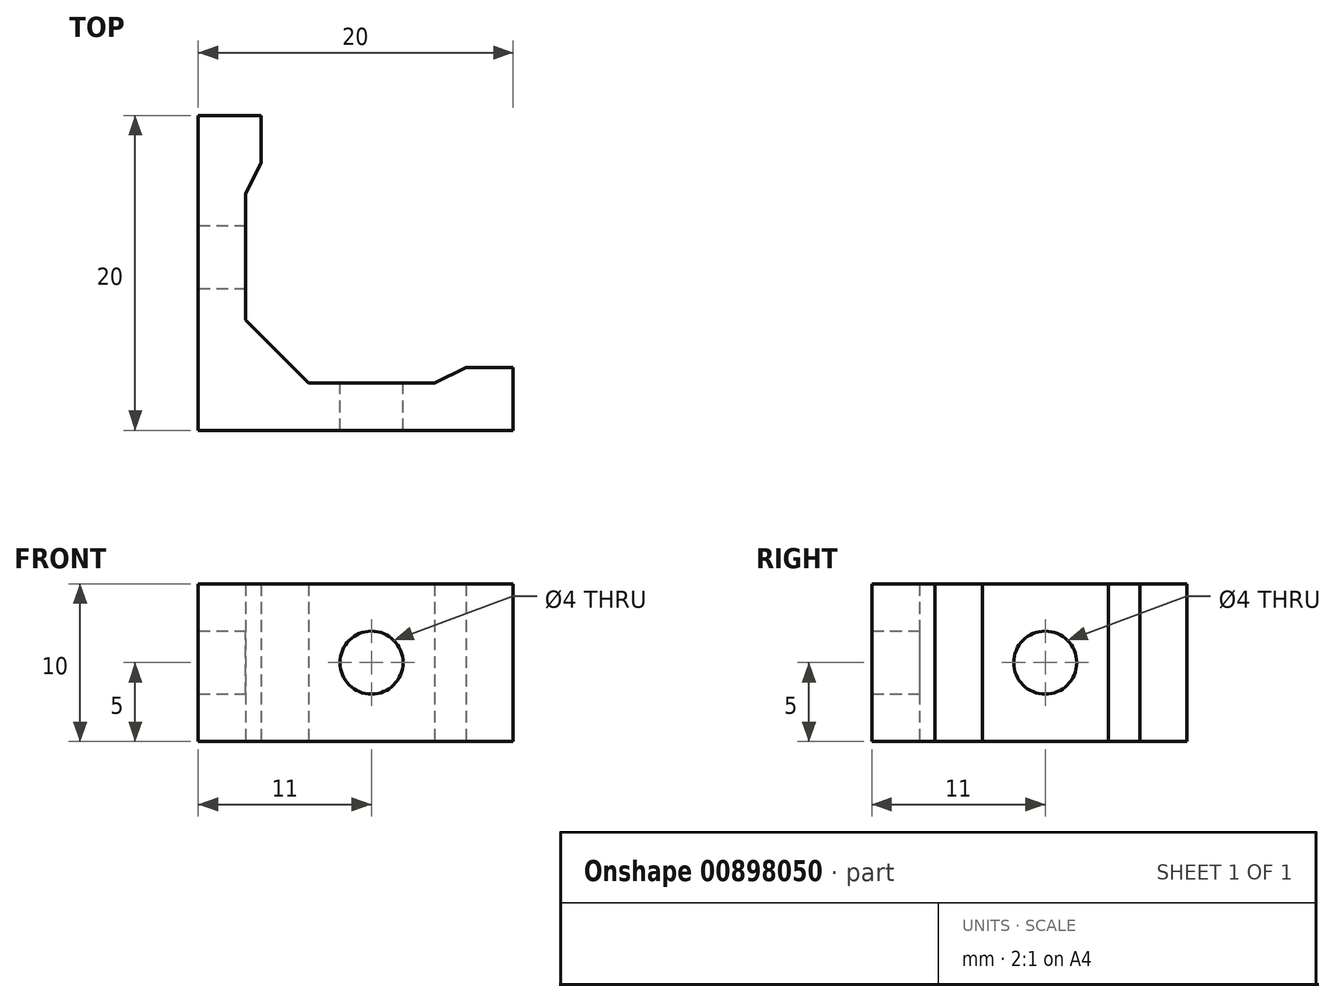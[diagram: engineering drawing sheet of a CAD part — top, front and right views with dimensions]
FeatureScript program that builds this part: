
annotation { "Feature Type Name" : "Feature", "Feature Type Description" : "" }
export const myFeature = defineFeature(function(context is Context, id is Id, definition is map)
    precondition{}
    {
        {
            var Q0;
            Q0=qCreatedBy(makeId("Top.planeOp"),FACE);
            var sketch = newSketch(context, id + "F0", { "sketchPlane" : qUnion([Q0])});
            skLineSegment(sketch, "E0", {"start": v(0, 0) * mm, "end": v(20, 0) * mm});
            skLineSegment(sketch, "E1", {"start": v(0, 0) * mm, "end": v(40, 40) * mm, "construction": true});
            skLineSegment(sketch, "E2", {"start": v(0, 0) * mm, "end": v(0, 40) * mm, "construction": true});
            skLineSegment(sketch, "E3", {"start": v(0, 40) * mm, "end": v(40, 40) * mm, "construction": true});
            skLineSegment(sketch, "E4", {"start": v(40, 40) * mm, "end": v(40, 0) * mm, "construction": true});
            skLineSegment(sketch, "E5", {"start": v(20, 0) * mm, "end": v(20, 4) * mm});
            skLineSegment(sketch, "E6", {"start": v(20, 4) * mm, "end": v(17, 4) * mm});
            skLineSegment(sketch, "E7", {"start": v(17, 4) * mm, "end": v(15, 3) * mm});
            skLineSegment(sketch, "E8", {"start": v(15, 3) * mm, "end": v(7, 3) * mm});
            skLineSegment(sketch, "E9", {"start": v(15, 3) * mm, "end": v(15, 0) * mm, "construction": true});
            skLineSegment(sketch, "E10", {"start": v(15, 3) * mm, "end": v(20, 3) * mm, "construction": true});
            skLineSegment(sketch, "E11", {"start": v(7, 3) * mm, "end": v(5, 5) * mm});
            skLineSegment(sketch, "E12.MirrorCS", {"start": v(3, 7) * mm, "end": v(5, 5) * mm});
            skLineSegment(sketch, "E13.MirrorCS", {"start": v(3, 15) * mm, "end": v(3, 7) * mm});
            skLineSegment(sketch, "E14.MirrorCS", {"start": v(4, 17) * mm, "end": v(3, 15) * mm});
            skLineSegment(sketch, "E15.MirrorCS", {"start": v(4, 20) * mm, "end": v(4, 17) * mm});
            skLineSegment(sketch, "E16.MirrorCS", {"start": v(0, 0) * mm, "end": v(0, 20) * mm});
            skLineSegment(sketch, "E17.MirrorCS", {"start": v(0, 20) * mm, "end": v(4, 20) * mm});
            skSolve(sketch);
        }
        {
            var Q0;
            Q0=makeQuery(id+"F0.imprint","IMPRINT",FACE,{"disambiguationData":[TD([[makeQuery(id+"F0.imprint","IMPRINT",EDGE,{"derivedFrom":sQuery(id+"F0.wireOp",EDGE,"E0")}),1.0]])]});
            extrude(context, id + "F1", {"entities" : qUnion([Q0]), "depth" : 10 * mm, "offsetDistance" : 25 * mm});
        }
        {
            var Q0;
            Q0=makeQuery(id+"F1.opExtrude","SWEPT_FACE",FACE,{"disambiguationData":[OSD([sQuery(id+"F0.wireOp",EDGE,"E13.MirrorCS")])]});
            var sketch = newSketch(context, id + "F2", { "sketchPlane" : qUnion([Q0])});
            skLineSegment(sketch, "E18", {"start": v(0, 0) * mm, "end": v(0, 5) * mm, "construction": true});
            skLineSegment(sketch, "E19", {"start": v(0, 5) * mm, "end": v(11, 5) * mm, "construction": true});
            skCircle(sketch, "E20", {"center": v(11, 5) * mm, "radius": 2 * mm});
            skSolve(sketch);
        }
        {
            var Q0;
            Q0=qSketchRegion(id+"F2",true);
            extrude(context, id + "F3", {"entities" : qUnion([Q0]), "operationType" : NewBodyOperationType.REMOVE, "oppositeDirection" : true, "depth" : 5 * mm, "offsetDistance" : 25 * mm});
        }
        {
            var Q0;
            Q0=makeQuery(id+"F1.opExtrude","SWEPT_FACE",FACE,{"disambiguationData":[OSD([sQuery(id+"F0.wireOp",EDGE,"E8")])]});
            var sketch = newSketch(context, id + "F4", { "sketchPlane" : qUnion([Q0])});
            skLineSegment(sketch, "E21", {"start": v(0, 0) * mm, "end": v(0, 5) * mm, "construction": true});
            skLineSegment(sketch, "E22", {"start": v(0, 5) * mm, "end": v(-11, 5) * mm, "construction": true});
            skCircle(sketch, "E23", {"center": v(-11, 5) * mm, "radius": 2 * mm});
            skSolve(sketch);
        }
        {
            var Q0;
            Q0=qSketchRegion(id+"F4",true);
            extrude(context, id + "F5", {"entities" : qUnion([Q0]), "operationType" : NewBodyOperationType.REMOVE, "oppositeDirection" : true, "depth" : 5 * mm, "offsetDistance" : 25 * mm});
        }
    });
